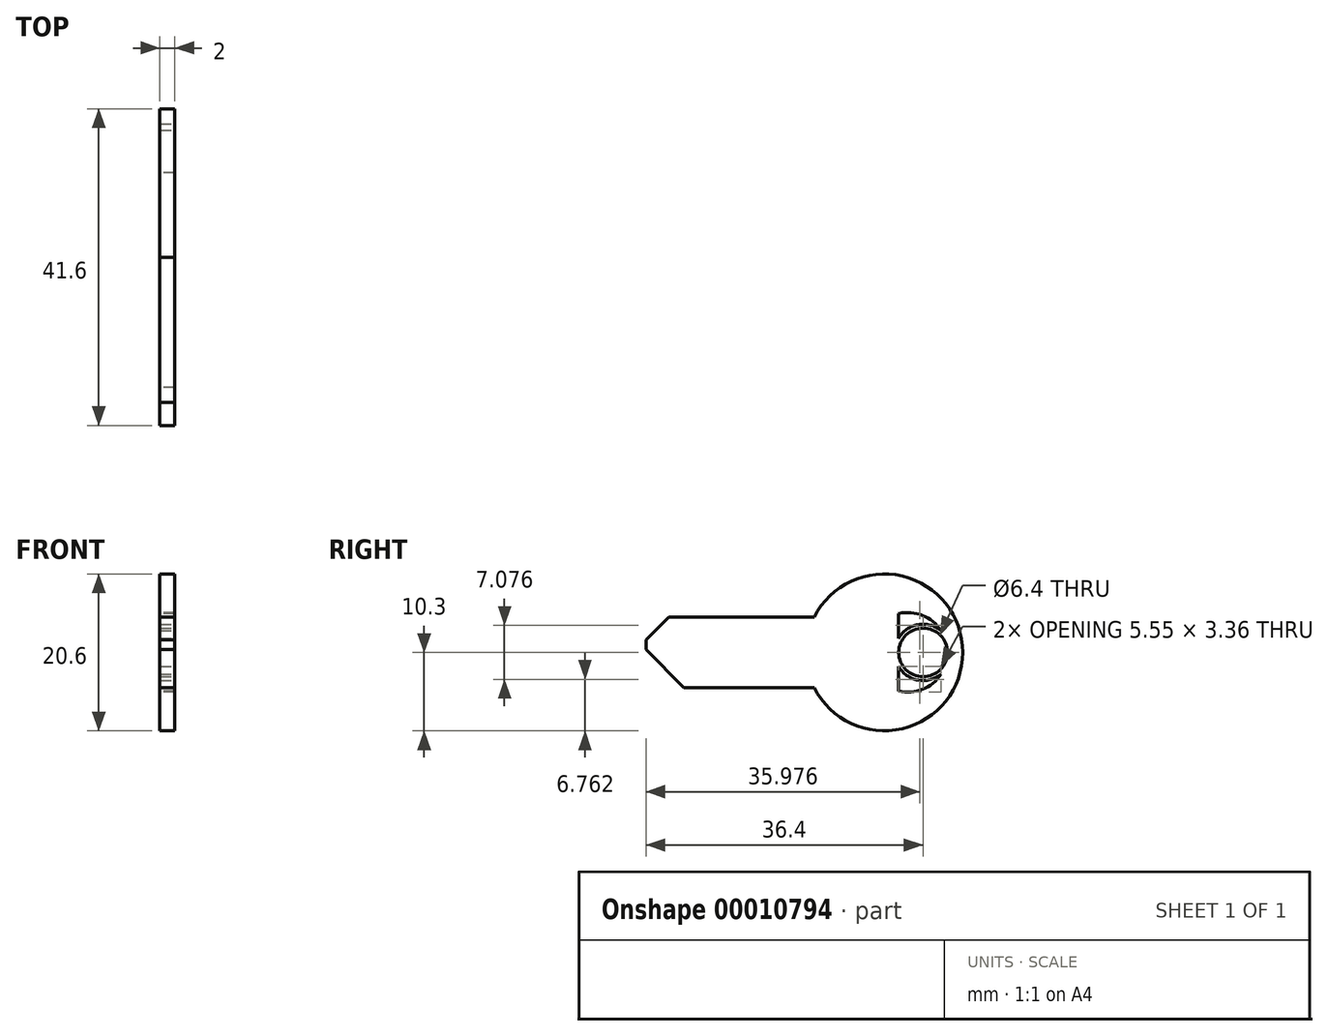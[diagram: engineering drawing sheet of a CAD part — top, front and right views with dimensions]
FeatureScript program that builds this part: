
annotation { "Feature Type Name" : "Feature", "Feature Type Description" : "" }
export const myFeature = defineFeature(function(context is Context, id is Id, definition is map)
    precondition{}
    {
        {
            var Q0;
            Q0=qCreatedBy(makeId("Right.planeOp"),FACE);
            var sketch = newSketch(context, id + "F0", { "sketchPlane" : qUnion([Q0])});
            skCircle(sketch, "E0", {"center": v(0, 0) * mm, "radius": 3.2 * mm, "construction": true});
            skArc(sketch, "E1", {"start": v(-3.2, -5.1) * mm, "mid": v(3.2, 0) * mm, "end": v(-3.2, 5.1) * mm});
            skLineSegment(sketch, "E2", {"start": v(0, 0) * mm, "end": v(-10.2, 0) * mm, "construction": true});
            skLineSegment(sketch, "E3", {"start": v(-3.2, 5.1) * mm, "end": v(-3.2, -5.1) * mm});
            skCircle(sketch, "E4", {"center": v(-5.1, 0) * mm, "radius": 10.3 * mm});
            skLineSegment(sketch, "E5", {"start": v(-14.3, 4.62) * mm, "end": v(-36.4, 4.62) * mm});
            skLineSegment(sketch, "E6", {"start": v(-36.4, 4.62) * mm, "end": v(-36.4, -4.63) * mm});
            skLineSegment(sketch, "E7", {"start": v(-36.4, -4.63) * mm, "end": v(-14.3, -4.63) * mm});
            skSolve(sketch);
        }
        {
            var Q0;
            Q0 = qSketchRegion(id + "F0", true);
            extrude(context, id + "F1", {"entities" : qUnion([Q0]), "depth" : 2 * mm, "symmetric" : true});
        }
        {
            var Q0;
            Q0=makeQuery(id+"F1.opExtrude","CAP_FACE",FACE,{"disambiguationData":[OSD([sQuery(id+"F0.wireOp",EDGE,"E1"),sQuery(id+"F0.wireOp",EDGE,"E3"),sQuery(id+"F0.wireOp",EDGE,"E4"),sQuery(id+"F0.wireOp",EDGE,"E5"),sQuery(id+"F0.wireOp",EDGE,"E6"),sQuery(id+"F0.wireOp",EDGE,"E7")])],"isStart":false});
            var sketch = newSketch(context, id + "F2", { "sketchPlane" : qUnion([Q0])});
            skCircle(sketch, "E8.0", {"center": v(0, 0) * mm, "radius": 3.2 * mm});
            skCircle(sketch, "E9", {"center": v(0, 0) * mm, "radius": 3.7 * mm});
            skSolve(sketch);
        }
        {
            var Q0;
            Q0 = qSketchRegion(id + "F2", true);
            var Q1;
            Q1=makeQuery(id+"F1.opExtrude","CAP_FACE",FACE,{"disambiguationData":[OSD([sQuery(id+"F0.wireOp",EDGE,"E1"),sQuery(id+"F0.wireOp",EDGE,"E3"),sQuery(id+"F0.wireOp",EDGE,"E4"),sQuery(id+"F0.wireOp",EDGE,"E5"),sQuery(id+"F0.wireOp",EDGE,"E6"),sQuery(id+"F0.wireOp",EDGE,"E7")])],"isStart":true});
            extrude(context, id + "F3", {"entities" : qUnion([Q0]), "operationType" : NewBodyOperationType.ADD, "endBound" : BoundingType.UP_TO_SURFACE, "oppositeDirection" : true, "endBoundEntityFace" : qUnion([Q1]), "depth" : 25 * mm});
        }
        {
            var Q0;
            Q0=makeQuery(id+"F1.opExtrude","SWEPT_EDGE",EDGE,{"disambiguationData":[OSD([sQuery(id+"F0.wireOp",EDGE,"E5"),sQuery(id+"F0.wireOp",EDGE,"E6")])]});
            chamfer(context, id + "F4", {"entities" : qUnion([Q0]), "width" : 3 * mm, "tangentPropagation" : true});
        }
        {
            var Q0;
            Q0=makeQuery(id+"F1.opExtrude","SWEPT_EDGE",EDGE,{"disambiguationData":[OSD([sQuery(id+"F0.wireOp",EDGE,"E6"),sQuery(id+"F0.wireOp",EDGE,"E7")])]});
            chamfer(context, id + "F5", {"entities" : qUnion([Q0]), "width" : 5 * mm, "tangentPropagation" : true});
        }
    });
